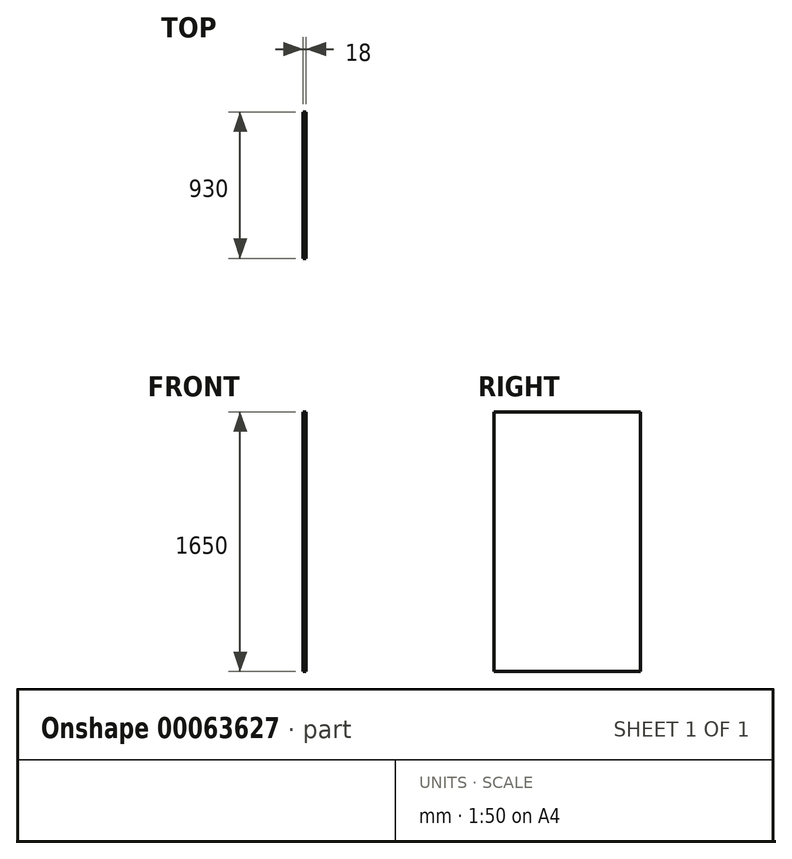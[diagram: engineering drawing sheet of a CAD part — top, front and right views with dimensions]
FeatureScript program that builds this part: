
annotation { "Feature Type Name" : "Feature", "Feature Type Description" : "" }
export const myFeature = defineFeature(function(context is Context, id is Id, definition is map)
    precondition{}
    {
        {
            var Q0;
            Q0=qCreatedBy(makeId("Right.planeOp"),FACE);
            var sketch = newSketch(context, id + "F0", { "sketchPlane" : qUnion([Q0])});
            skLineSegment(sketch, "E0.bottom", {"start": v(0, 0) * mm, "end": v(930, 0) * mm});
            skLineSegment(sketch, "E0.top", {"start": v(0, -1650) * mm, "end": v(930, -1650) * mm});
            skLineSegment(sketch, "E0.left", {"start": v(0, 0) * mm, "end": v(0, -1650) * mm});
            skLineSegment(sketch, "E0.right", {"start": v(930, 0) * mm, "end": v(930, -1650) * mm});
            skSolve(sketch);
        }
        {
            var Q0;
            Q0=makeQuery(id+"F0.imprint","IMPRINT",FACE,{"disambiguationData":[TD([[makeQuery(id+"F0.imprint","IMPRINT",EDGE,{"derivedFrom":sQuery(id+"F0.wireOp",EDGE,"E0.bottom")}),-1.0]])]});
            extrude(context, id + "F1", {"entities" : qUnion([Q0]), "depth" : 18 * mm});
        }
    });
